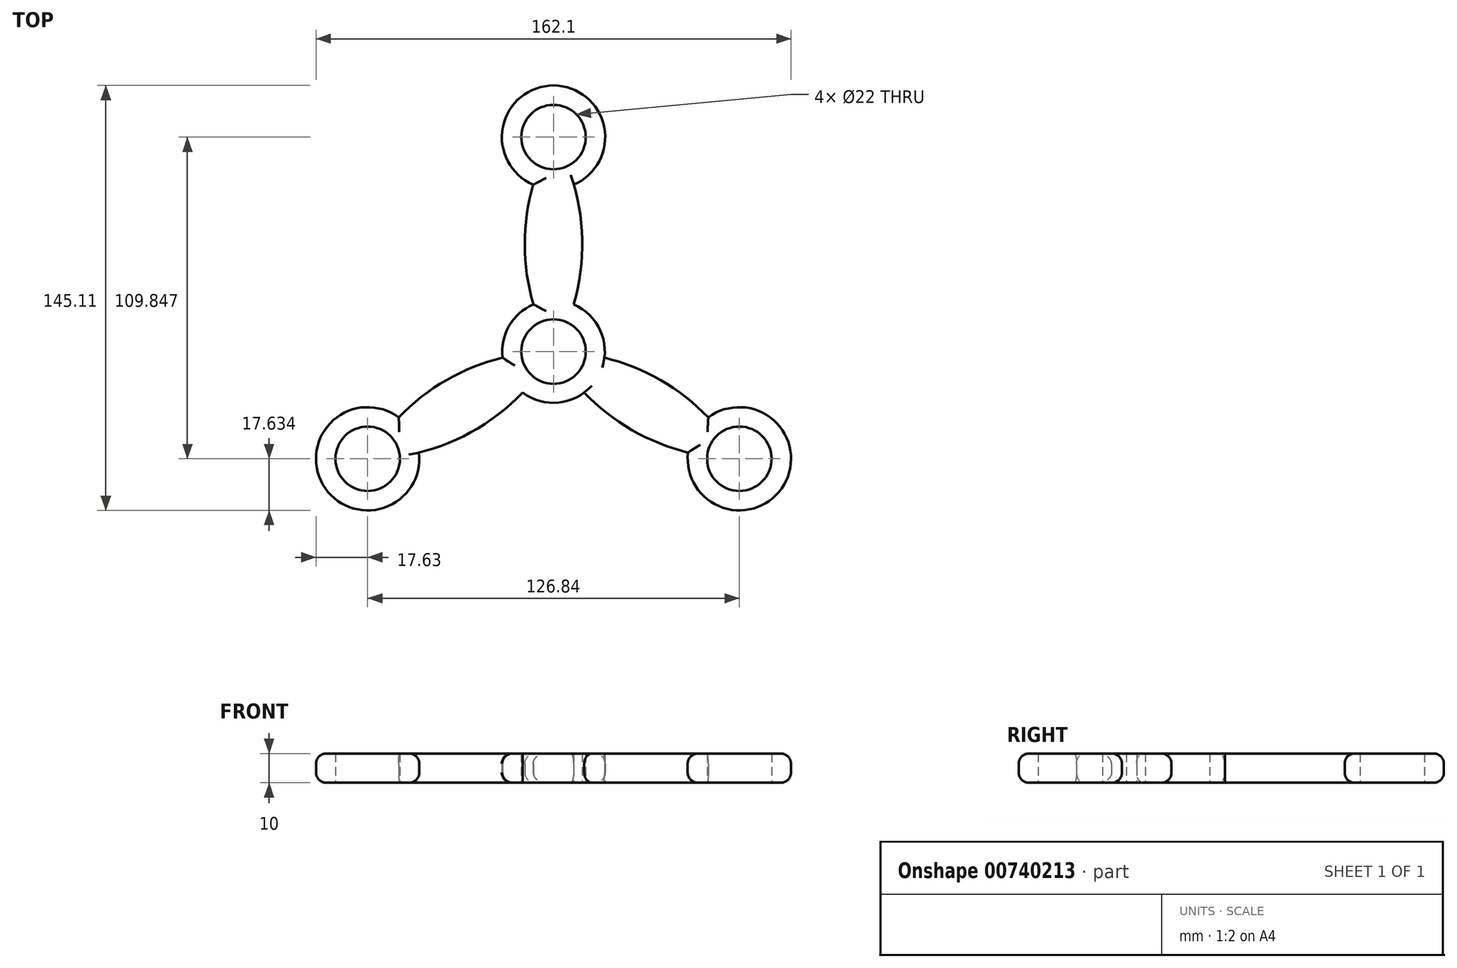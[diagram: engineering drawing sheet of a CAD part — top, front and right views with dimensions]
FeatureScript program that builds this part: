
annotation { "Feature Type Name" : "Feature", "Feature Type Description" : "" }
export const myFeature = defineFeature(function(context is Context, id is Id, definition is map)
    precondition{}
    {
        {
            var Q0;
            Q0=qCreatedBy(makeId("Top.planeOp"),FACE);
            var sketch = newSketch(context, id + "F0", { "sketchPlane" : qUnion([Q0])});
            skCircle(sketch, "E0", {"center": v(0, 0) * mm, "radius": 4 * mm});
            skCircle(sketch, "E1", {"center": v(0, 0) * mm, "radius": 11 * mm});
            skCircle(sketch, "E2", {"center": v(0, 0) * mm, "radius": 17.5 * mm});
            skCircle(sketch, "E3", {"center": v(0, 73.23) * mm, "radius": 4 * mm});
            skCircle(sketch, "E4", {"center": v(0, 73.23) * mm, "radius": 11 * mm});
            skCircle(sketch, "E5", {"center": v(0, 73.23) * mm, "radius": 17.63 * mm});
            skCircle(sketch, "E6.1.0", {"center": v(-63.42, -36.62) * mm, "radius": 4 * mm});
            skCircle(sketch, "E6.1.1", {"center": v(-63.42, -36.62) * mm, "radius": 11 * mm});
            skCircle(sketch, "E6.1.2", {"center": v(-63.42, -36.62) * mm, "radius": 17.63 * mm});
            skCircle(sketch, "E6.2.0", {"center": v(63.42, -36.62) * mm, "radius": 4 * mm});
            skCircle(sketch, "E6.2.1", {"center": v(63.42, -36.62) * mm, "radius": 11 * mm});
            skCircle(sketch, "E6.2.2", {"center": v(63.42, -36.62) * mm, "radius": 17.63 * mm});
            skLineSegment(sketch, "E7", {"start": v(0, 55.6) * mm, "end": v(0, 17.5) * mm});
            skLineSegment(sketch, "E8", {"start": v(15.16, -8.75) * mm, "end": v(48.15, -27.8) * mm});
            skLineSegment(sketch, "E9", {"start": v(0, 17.5) * mm, "end": v(0, 55.6) * mm});
            skLineSegment(sketch, "E10", {"start": v(-15.16, -8.75) * mm, "end": v(-48.15, -27.8) * mm});
            skCircle(sketch, "E11", {"center": v(0, 0) * mm, "radius": 73.23 * mm, "construction": true});
            skLineSegment(sketch, "E12", {"start": v(-39.25, -22.66) * mm, "end": v(-59.96, -34.62) * mm});
            skArc(sketch, "E13", {"start": v(0, 73.23) * mm, "mid": v(0, 0) * mm, "end": v(63.42, -36.62) * mm});
            skArc(sketch, "E14", {"start": v(-63.42, -36.62) * mm, "mid": v(0, 0) * mm, "end": v(0, 73.23) * mm});
            skArc(sketch, "E15", {"start": v(63.42, -36.62) * mm, "mid": v(0, 0) * mm, "end": v(-63.42, -36.62) * mm});
            skSolve(sketch);
        }
        {
            var Q0;
            Q0 = qSketchRegion(id + "F0", true);
            extrude(context, id + "F1", {"entities" : qUnion([Q0]), "depth" : 10 * mm, "offsetDistance" : 25.4 * mm});
        }
        {
            var Q0;
            Q0=makeQuery(id+"F1.opExtrude","CAP_EDGE",EDGE,{"disambiguationData":[OSD([sQuery(id+"F0.wireOp",EDGE,"E5")])],"isStart":false});
            var Q1;
            {var subQ0=sQuery(id+"F0.wireOp",EDGE,"E13");Q1=makeQuery(id+"F1.opExtrude","CAP_EDGE",EDGE,{"disambiguationData":[OSD([subQ0]),TDD([makeQuery(id+"F0.imprint","IMPRINT",EDGE,{"disambiguationData":[TD([[makeQuery(id+"F0.imprint","INTERSECT",VERTEX,{"disambiguationData":[OD(0.0)],"derivedFrom":[sQuery(id+"F0.wireOp",EDGE,"E2"),subQ0]}),1.0]])],"derivedFrom":subQ0})])],"isStart":false});}
            var Q2;
            {var subQ0=sQuery(id+"F0.wireOp",EDGE,"E14");Q2=makeQuery(id+"F1.opExtrude","CAP_EDGE",EDGE,{"disambiguationData":[OSD([subQ0]),TDD([makeQuery(id+"F0.imprint","IMPRINT",EDGE,{"disambiguationData":[TD([[makeQuery(id+"F0.imprint","INTERSECT",VERTEX,{"disambiguationData":[OD(0.0)],"derivedFrom":[sQuery(id+"F0.wireOp",EDGE,"E2"),subQ0]}),-1.0]])],"derivedFrom":subQ0})])],"isStart":false});}
            var Q3;
            {var subQ0=sQuery(id+"F0.wireOp",EDGE,"E2");Q3=makeQuery(id+"F1.opExtrude","CAP_EDGE",EDGE,{"disambiguationData":[OSD([subQ0]),TDD([makeQuery(id+"F0.imprint","IMPRINT",EDGE,{"disambiguationData":[TD([[makeQuery(id+"F0.imprint","INTERSECT",VERTEX,{"disambiguationData":[OD(0.0)],"derivedFrom":[subQ0,sQuery(id+"F0.wireOp",EDGE,"E14")]}),1.0]])],"derivedFrom":subQ0})])],"isStart":false});}
            var Q4;
            {var subQ0=sQuery(id+"F0.wireOp",EDGE,"E15");Q4=makeQuery(id+"F1.opExtrude","CAP_EDGE",EDGE,{"disambiguationData":[OSD([subQ0]),TDD([makeQuery(id+"F0.imprint","IMPRINT",EDGE,{"disambiguationData":[TD([[makeQuery(id+"F0.imprint","INTERSECT",VERTEX,{"disambiguationData":[OD(1.0)],"derivedFrom":[sQuery(id+"F0.wireOp",EDGE,"E2"),subQ0]}),1.0]])],"derivedFrom":subQ0})])],"isStart":false});}
            var Q5;
            {var subQ0=sQuery(id+"F0.wireOp",EDGE,"E13");Q5=makeQuery(id+"F1.opExtrude","CAP_EDGE",EDGE,{"disambiguationData":[OSD([subQ0]),TDD([makeQuery(id+"F0.imprint","IMPRINT",EDGE,{"disambiguationData":[TD([[makeQuery(id+"F0.imprint","INTERSECT",VERTEX,{"disambiguationData":[OD(1.0)],"derivedFrom":[sQuery(id+"F0.wireOp",EDGE,"E2"),subQ0]}),-1.0]])],"derivedFrom":subQ0})])],"isStart":false});}
            var Q6;
            {var subQ0=sQuery(id+"F0.wireOp",EDGE,"E2");Q6=makeQuery(id+"F1.opExtrude","CAP_EDGE",EDGE,{"disambiguationData":[OSD([subQ0]),TDD([makeQuery(id+"F0.imprint","IMPRINT",EDGE,{"disambiguationData":[TD([[makeQuery(id+"F0.imprint","INTERSECT",VERTEX,{"disambiguationData":[OD(1.0)],"derivedFrom":[subQ0,sQuery(id+"F0.wireOp",EDGE,"E14")]}),-1.0]])],"derivedFrom":subQ0})])],"isStart":false});}
            var Q7;
            {var subQ0=sQuery(id+"F0.wireOp",EDGE,"E2");Q7=makeQuery(id+"F1.opExtrude","CAP_EDGE",EDGE,{"disambiguationData":[OSD([subQ0]),TDD([makeQuery(id+"F0.imprint","IMPRINT",EDGE,{"disambiguationData":[TD([[makeQuery(id+"F0.imprint","INTERSECT",VERTEX,{"disambiguationData":[OD(0.0)],"derivedFrom":[subQ0,sQuery(id+"F0.wireOp",EDGE,"E13")]}),-1.0]])],"derivedFrom":subQ0})])],"isStart":false});}
            var Q8;
            {var subQ0=sQuery(id+"F0.wireOp",EDGE,"E15");Q8=makeQuery(id+"F1.opExtrude","CAP_EDGE",EDGE,{"disambiguationData":[OSD([subQ0]),TDD([makeQuery(id+"F0.imprint","IMPRINT",EDGE,{"disambiguationData":[TD([[makeQuery(id+"F0.imprint","INTERSECT",VERTEX,{"disambiguationData":[OD(0.0)],"derivedFrom":[sQuery(id+"F0.wireOp",EDGE,"E2"),subQ0]}),-1.0]])],"derivedFrom":subQ0})])],"isStart":false});}
            var Q9;
            {var subQ0=sQuery(id+"F0.wireOp",EDGE,"E14");Q9=makeQuery(id+"F1.opExtrude","CAP_EDGE",EDGE,{"disambiguationData":[OSD([subQ0]),TDD([makeQuery(id+"F0.imprint","IMPRINT",EDGE,{"disambiguationData":[TD([[makeQuery(id+"F0.imprint","INTERSECT",VERTEX,{"disambiguationData":[OD(1.0)],"derivedFrom":[sQuery(id+"F0.wireOp",EDGE,"E2"),subQ0]}),1.0]])],"derivedFrom":subQ0})])],"isStart":false});}
            var Q10;
            Q10=makeQuery(id+"F1.opExtrude","CAP_EDGE",EDGE,{"disambiguationData":[OSD([sQuery(id+"F0.wireOp",EDGE,"E6.1.2")])],"isStart":false});
            var Q11;
            Q11=makeQuery(id+"F1.opExtrude","CAP_EDGE",EDGE,{"disambiguationData":[OSD([sQuery(id+"F0.wireOp",EDGE,"E6.2.2")])],"isStart":false});
            var Q12;
            {var subQ0=sQuery(id+"F0.wireOp",EDGE,"E2");Q12=makeQuery(id+"F1.opExtrude","CAP_EDGE",EDGE,{"disambiguationData":[OSD([subQ0]),TDD([makeQuery(id+"F0.imprint","IMPRINT",EDGE,{"disambiguationData":[TD([[makeQuery(id+"F0.imprint","INTERSECT",VERTEX,{"disambiguationData":[OD(1.0)],"derivedFrom":[subQ0,sQuery(id+"F0.wireOp",EDGE,"E14")]}),-1.0]])],"derivedFrom":subQ0})])],"isStart":true});}
            var Q13;
            {var subQ0=sQuery(id+"F0.wireOp",EDGE,"E2");Q13=makeQuery(id+"F1.opExtrude","CAP_EDGE",EDGE,{"disambiguationData":[OSD([subQ0]),TDD([makeQuery(id+"F0.imprint","IMPRINT",EDGE,{"disambiguationData":[TD([[makeQuery(id+"F0.imprint","INTERSECT",VERTEX,{"disambiguationData":[OD(0.0)],"derivedFrom":[subQ0,sQuery(id+"F0.wireOp",EDGE,"E13")]}),-1.0]])],"derivedFrom":subQ0})])],"isStart":true});}
            var Q14;
            {var subQ0=sQuery(id+"F0.wireOp",EDGE,"E14");Q14=makeQuery(id+"F1.opExtrude","CAP_EDGE",EDGE,{"disambiguationData":[OSD([subQ0]),TDD([makeQuery(id+"F0.imprint","IMPRINT",EDGE,{"disambiguationData":[TD([[makeQuery(id+"F0.imprint","INTERSECT",VERTEX,{"disambiguationData":[OD(0.0)],"derivedFrom":[sQuery(id+"F0.wireOp",EDGE,"E2"),subQ0]}),-1.0]])],"derivedFrom":subQ0})])],"isStart":true});}
            var Q15;
            Q15=makeQuery(id+"F1.opExtrude","CAP_EDGE",EDGE,{"disambiguationData":[OSD([sQuery(id+"F0.wireOp",EDGE,"E5")])],"isStart":true});
            var Q16;
            {var subQ0=sQuery(id+"F0.wireOp",EDGE,"E13");Q16=makeQuery(id+"F1.opExtrude","CAP_EDGE",EDGE,{"disambiguationData":[OSD([subQ0]),TDD([makeQuery(id+"F0.imprint","IMPRINT",EDGE,{"disambiguationData":[TD([[makeQuery(id+"F0.imprint","INTERSECT",VERTEX,{"disambiguationData":[OD(0.0)],"derivedFrom":[sQuery(id+"F0.wireOp",EDGE,"E2"),subQ0]}),1.0]])],"derivedFrom":subQ0})])],"isStart":true});}
            var Q17;
            {var subQ0=sQuery(id+"F0.wireOp",EDGE,"E15");Q17=makeQuery(id+"F1.opExtrude","CAP_EDGE",EDGE,{"disambiguationData":[OSD([subQ0]),TDD([makeQuery(id+"F0.imprint","IMPRINT",EDGE,{"disambiguationData":[TD([[makeQuery(id+"F0.imprint","INTERSECT",VERTEX,{"disambiguationData":[OD(1.0)],"derivedFrom":[sQuery(id+"F0.wireOp",EDGE,"E2"),subQ0]}),1.0]])],"derivedFrom":subQ0})])],"isStart":true});}
            var Q18;
            {var subQ0=sQuery(id+"F0.wireOp",EDGE,"E14");Q18=makeQuery(id+"F1.opExtrude","CAP_EDGE",EDGE,{"disambiguationData":[OSD([subQ0]),TDD([makeQuery(id+"F0.imprint","IMPRINT",EDGE,{"disambiguationData":[TD([[makeQuery(id+"F0.imprint","INTERSECT",VERTEX,{"disambiguationData":[OD(1.0)],"derivedFrom":[sQuery(id+"F0.wireOp",EDGE,"E2"),subQ0]}),1.0]])],"derivedFrom":subQ0})])],"isStart":true});}
            var Q19;
            {var subQ0=sQuery(id+"F0.wireOp",EDGE,"E15");Q19=makeQuery(id+"F1.opExtrude","CAP_EDGE",EDGE,{"disambiguationData":[OSD([subQ0]),TDD([makeQuery(id+"F0.imprint","IMPRINT",EDGE,{"disambiguationData":[TD([[makeQuery(id+"F0.imprint","INTERSECT",VERTEX,{"disambiguationData":[OD(0.0)],"derivedFrom":[sQuery(id+"F0.wireOp",EDGE,"E2"),subQ0]}),-1.0]])],"derivedFrom":subQ0})])],"isStart":true});}
            var Q20;
            Q20=makeQuery(id+"F1.opExtrude","CAP_EDGE",EDGE,{"disambiguationData":[OSD([sQuery(id+"F0.wireOp",EDGE,"E6.1.2")])],"isStart":true});
            var Q21;
            Q21=makeQuery(id+"F1.opExtrude","CAP_EDGE",EDGE,{"disambiguationData":[OSD([sQuery(id+"F0.wireOp",EDGE,"E6.2.2")])],"isStart":true});
            var Q22;
            {var subQ0=sQuery(id+"F0.wireOp",EDGE,"E2");Q22=makeQuery(id+"F1.opExtrude","CAP_EDGE",EDGE,{"disambiguationData":[OSD([subQ0]),TDD([makeQuery(id+"F0.imprint","IMPRINT",EDGE,{"disambiguationData":[TD([[makeQuery(id+"F0.imprint","INTERSECT",VERTEX,{"disambiguationData":[OD(0.0)],"derivedFrom":[subQ0,sQuery(id+"F0.wireOp",EDGE,"E14")]}),1.0]])],"derivedFrom":subQ0})])],"isStart":true});}
            var Q23;
            {var subQ0=sQuery(id+"F0.wireOp",EDGE,"E13");Q23=makeQuery(id+"F1.opExtrude","CAP_EDGE",EDGE,{"disambiguationData":[OSD([subQ0]),TDD([makeQuery(id+"F0.imprint","IMPRINT",EDGE,{"disambiguationData":[TD([[makeQuery(id+"F0.imprint","INTERSECT",VERTEX,{"disambiguationData":[OD(1.0)],"derivedFrom":[sQuery(id+"F0.wireOp",EDGE,"E2"),subQ0]}),-1.0]])],"derivedFrom":subQ0})])],"isStart":true});}
            fillet(context, id + "F2", {"entities" : qUnion([Q0, Q1, Q2, Q3, Q4, Q5, Q6, Q7, Q8, Q9, Q10, Q11, Q12, Q13, Q14, Q15, Q16, Q17, Q18, Q19, Q20, Q21, Q22, Q23]), "radius" : 3.5 * mm, "tangentPropagation" : true, "allowEdgeOverflow" : false});
        }
    });
